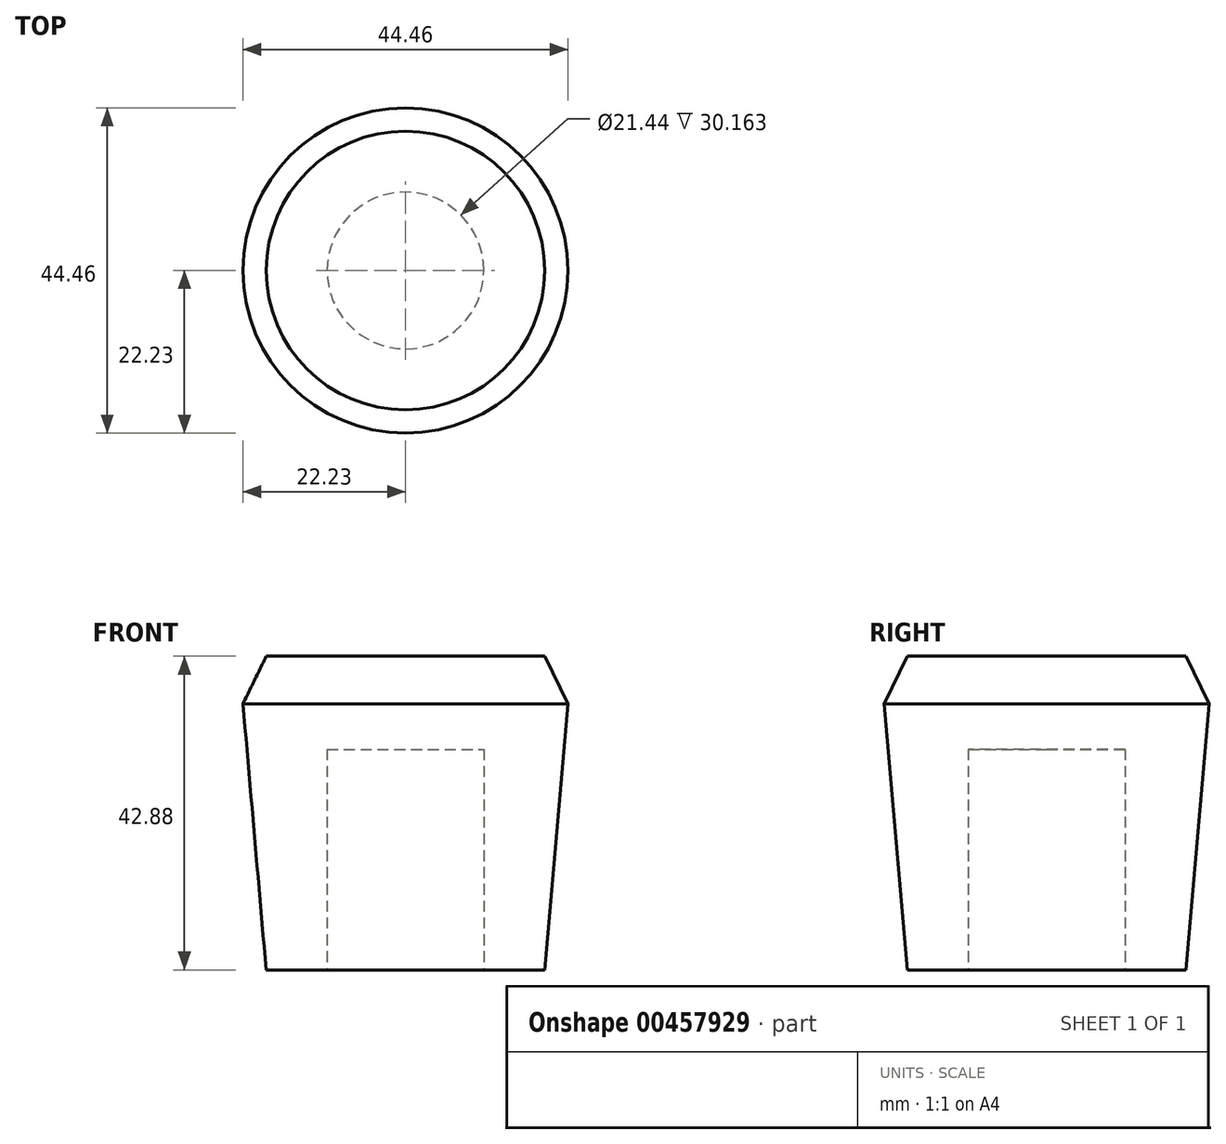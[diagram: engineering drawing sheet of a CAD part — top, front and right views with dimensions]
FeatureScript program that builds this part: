
annotation { "Feature Type Name" : "Feature", "Feature Type Description" : "" }
export const myFeature = defineFeature(function(context is Context, id is Id, definition is map)
    precondition{}
    {
        {
            var Q0;
            Q0=qCreatedBy(makeId("Front.planeOp"),FACE);
            var sketch = newSketch(context, id + "F0", { "sketchPlane" : qUnion([Q0])});
            skLineSegment(sketch, "E0", {"start": v(0, 0) * mm, "end": v(0, 42.88) * mm});
            skLineSegment(sketch, "E1", {"start": v(0, 0) * mm, "end": v(-19.05, 0) * mm});
            skLineSegment(sketch, "E2", {"start": v(-19.05, 0) * mm, "end": v(-22.23, 0) * mm, "construction": true});
            skLineSegment(sketch, "E3", {"start": v(-19.05, 0) * mm, "end": v(-22.23, 36.37) * mm});
            skLineSegment(sketch, "E4", {"start": v(-22.23, 36.37) * mm, "end": v(-19.04, 42.88) * mm});
            skLineSegment(sketch, "E5", {"start": v(-19.04, 42.88) * mm, "end": v(0, 42.88) * mm});
            skPoint(sketch, "E6.orphan", {"position": v(-22.23, 42.88) * mm});
            skPoint(sketch, "E7.end.orphan", {"position": v(-19.04, 36.37) * mm});
            skSolve(sketch);
        }
        {
            var Q0;
            Q0=makeQuery(id+"F0.imprint","IMPRINT",FACE,{"disambiguationData":[TD([[makeQuery(id+"F0.imprint","IMPRINT",EDGE,{"derivedFrom":sQuery(id+"F0.wireOp",EDGE,"E0")}),1.0]])]});
            var Q1;
            Q1=sQuery(id+"F0.wireOp",EDGE,"E0");
            revolve(context, id + "F1", {"entities" : qUnion([Q0]), "axis" : qUnion([Q1]), "revolveType" : RevolveType.FULL});
        }
        {
            var Q0;
            Q0=makeQuery(id+"F1.opRevolve","SWEPT_FACE",FACE,{"disambiguationData":[OSD([sQuery(id+"F0.wireOp",EDGE,"E1")])]});
            var sketch = newSketch(context, id + "F2", { "sketchPlane" : qUnion([Q0])});
            skCircle(sketch, "E8", {"center": v(0, 0) * mm, "radius": 10.72 * mm});
            skSolve(sketch);
        }
        {
            var Q0;
            Q0=makeQuery(id+"F2.imprint","IMPRINT",FACE,{"disambiguationData":[TD([[makeQuery(id+"F2.imprint","IMPRINT",EDGE,{"derivedFrom":sQuery(id+"F2.wireOp",EDGE,"E8")}),1.0]])]});
            extrude(context, id + "F3", {"entities" : qUnion([Q0]), "operationType" : NewBodyOperationType.REMOVE, "oppositeDirection" : true, "depth" : 30.16 * mm});
        }
    });
